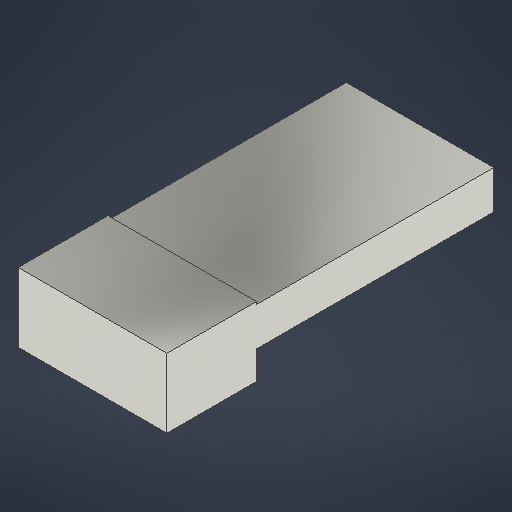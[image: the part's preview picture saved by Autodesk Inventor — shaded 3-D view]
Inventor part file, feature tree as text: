
AUTODESK INVENTOR PART (.ipt)
format: ipt  version: 2025.1 (Build 291241000, 241)  size: 252,928 bytes
history: native  units: in
note: dims shown in document units (in); Inventor stores cm internally (conversion verified against a paired STEP export)
features: extrude x3, sketch x2, other x1
ambient origin geometry x8: Origin, YZ Plane, XZ Plane, XY Plane, X Axis, Y Axis, Z Axis, Center Point
bodies: Solid1 (feature_tree)
feature tree (6):
  extrude  "Extrusion1"  Depth=10.0394in
  sketch  "Sketch2"  dims[d2=1.1811in d3=0.0in d4=1.378in d5=4.6063in d6=0.0787in d7=0.0in d8=2.0472in d9=0.0in]
  extrude  "Extrusion2"  Depth=2.0472in
  extrude  "Extrusion3"  Depth=2.0472in
  sketch  "Sketch1"  dims[d0=4.5276in d1=10.0394in]
  other  "Finish1"
